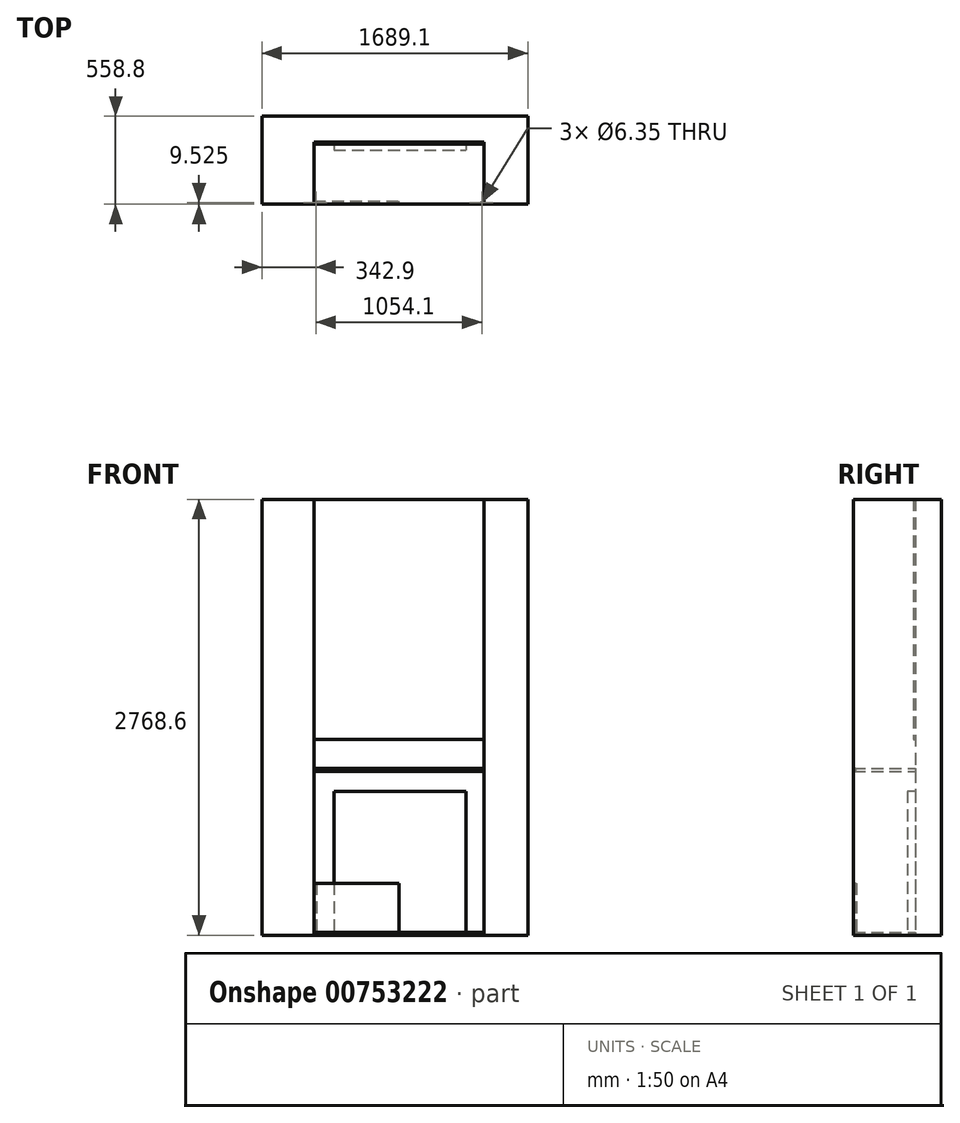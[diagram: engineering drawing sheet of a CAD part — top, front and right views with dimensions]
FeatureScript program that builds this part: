
annotation { "Feature Type Name" : "Feature", "Feature Type Description" : "" }
export const myFeature = defineFeature(function(context is Context, id is Id, definition is map)
    precondition{}
    {
        {
            var Q0;
            Q0=qCreatedBy(makeId("Top.planeOp"),FACE);
            var sketch = newSketch(context, id + "F0", { "sketchPlane" : qUnion([Q0])});
            skLineSegment(sketch, "E0", {"start": v(0, 0) * mm, "end": v(539.75, 0) * mm, "construction": true});
            skLineSegment(sketch, "E1", {"start": v(0, 0) * mm, "end": v(-539.75, 0) * mm, "construction": true});
            skLineSegment(sketch, "E2", {"start": v(-539.75, 393.7) * mm, "end": v(539.75, 393.7) * mm});
            skLineSegment(sketch, "E3", {"start": v(-539.75, 0) * mm, "end": v(-539.75, 393.7) * mm});
            skLineSegment(sketch, "E4", {"start": v(539.75, 393.7) * mm, "end": v(539.75, 0) * mm});
            skLineSegment(sketch, "E5", {"start": v(-539.75, 0) * mm, "end": v(-869.95, 0) * mm});
            skLineSegment(sketch, "E6", {"start": v(539.75, 0) * mm, "end": v(819.15, 0) * mm});
            skLineSegment(sketch, "E7", {"start": v(-869.95, 0) * mm, "end": v(-869.95, 558.8) * mm});
            skLineSegment(sketch, "E8", {"start": v(-869.95, 558.8) * mm, "end": v(819.15, 558.8) * mm});
            skLineSegment(sketch, "E9", {"start": v(819.15, 558.8) * mm, "end": v(819.15, 0) * mm});
            skSolve(sketch);
        }
        {
            var Q0;
            Q0 = qSketchRegion(id + "F0", true);
            extrude(context, id + "F1", {"entities" : qUnion([Q0]), "depth" : 2768.6 * mm, "offsetDistance" : 25.4 * mm});
        }
        {
            var Q0;
            Q0=makeQuery(id+"F0.imprint","IMPRINT",FACE,{"disambiguationData":[TD([[makeQuery(id+"F0.imprint","IMPRINT",EDGE,{"derivedFrom":sQuery(id+"F0.wireOp",EDGE,"E2")}),1.0]])]});
            var sketch = newSketch(context, id + "F2", { "sketchPlane" : qUnion([Q0])});
            skLineSegment(sketch, "E10.bottom", {"start": v(-539.75, 393.7) * mm, "end": v(539.75, 393.7) * mm});
            skLineSegment(sketch, "E10.top", {"start": v(-539.75, 381) * mm, "end": v(539.75, 381) * mm});
            skLineSegment(sketch, "E10.left", {"start": v(-539.75, 393.7) * mm, "end": v(-539.75, 381) * mm});
            skLineSegment(sketch, "E10.right", {"start": v(539.75, 393.7) * mm, "end": v(539.75, 381) * mm});
            skSolve(sketch);
        }
        {
            var Q0;
            Q0 = qSketchRegion(id + "F2", true);
            extrude(context, id + "F3", {"entities" : qUnion([Q0]), "depth" : 2768.6 * mm, "offsetDistance" : 25.4 * mm, "hasSecondDirection" : true, "secondDirectionOppositeDirection" : false, "secondDirectionDepth" : 1244.6 * mm});
        }
        {
            var Q0;
            Q0=makeQuery(id+"F0.imprint","IMPRINT",FACE,{"disambiguationData":[TD([[makeQuery(id+"F0.imprint","IMPRINT",EDGE,{"derivedFrom":sQuery(id+"F0.wireOp",EDGE,"E2")}),1.0]])]});
            var sketch = newSketch(context, id + "F4", { "sketchPlane" : qUnion([Q0])});
            skLineSegment(sketch, "E11.bottom", {"start": v(-539.75, 393.7) * mm, "end": v(539.75, 393.7) * mm});
            skLineSegment(sketch, "E11.top", {"start": v(-539.75, 0) * mm, "end": v(539.75, 0) * mm});
            skLineSegment(sketch, "E11.left", {"start": v(-539.75, 393.7) * mm, "end": v(-539.75, 0) * mm});
            skLineSegment(sketch, "E11.right", {"start": v(539.75, 393.7) * mm, "end": v(539.75, 0) * mm});
            skSolve(sketch);
        }
        {
            var Q0;
            Q0 = qSketchRegion(id + "F4", true);
            extrude(context, id + "F5", {"entities" : qUnion([Q0]), "depth" : 19.05 * mm, "offsetDistance" : 25.4 * mm});
        }
        {
            var Q0;
            Q0=makeQuery(id+"F0.imprint","IMPRINT",FACE,{"disambiguationData":[TD([[makeQuery(id+"F0.imprint","IMPRINT",EDGE,{"derivedFrom":sQuery(id+"F0.wireOp",EDGE,"E2")}),1.0]])]});
            var sketch = newSketch(context, id + "F6", { "sketchPlane" : qUnion([Q0])});
            skLineSegment(sketch, "E12.bottom", {"start": v(-412.75, 393.7) * mm, "end": v(425.45, 393.7) * mm});
            skLineSegment(sketch, "E12.top", {"start": v(-412.75, 342.9) * mm, "end": v(425.45, 342.9) * mm});
            skLineSegment(sketch, "E12.left", {"start": v(-412.75, 393.7) * mm, "end": v(-412.75, 342.9) * mm});
            skLineSegment(sketch, "E12.right", {"start": v(425.45, 393.7) * mm, "end": v(425.45, 342.9) * mm});
            skSolve(sketch);
        }
        {
            var Q0;
            Q0 = qSketchRegion(id + "F6", true);
            extrude(context, id + "F7", {"entities" : qUnion([Q0]), "depth" : 914.4 * mm, "offsetDistance" : 25.4 * mm});
        }
        {
            var Q0;
            Q0=makeQuery(id+"F0.imprint","IMPRINT",FACE,{"disambiguationData":[TD([[makeQuery(id+"F0.imprint","IMPRINT",EDGE,{"derivedFrom":sQuery(id+"F0.wireOp",EDGE,"E2")}),1.0]])]});
            var sketch = newSketch(context, id + "F8", { "sketchPlane" : qUnion([Q0])});
            skLineSegment(sketch, "E13.bottom", {"start": v(-539.75, 393.7) * mm, "end": v(539.75, 393.7) * mm});
            skLineSegment(sketch, "E13.top", {"start": v(-539.75, 0) * mm, "end": v(539.75, 0) * mm});
            skLineSegment(sketch, "E13.left", {"start": v(-539.75, 393.7) * mm, "end": v(-539.75, 0) * mm});
            skLineSegment(sketch, "E13.right", {"start": v(539.75, 393.7) * mm, "end": v(539.75, 0) * mm});
            skCircle(sketch, "E14", {"center": v(-527.05, 9.53) * mm, "radius": 3.18 * mm});
            skCircle(sketch, "E15.MirrorC", {"center": v(527.05, 9.53) * mm, "radius": 3.18 * mm});
            skSolve(sketch);
        }
        {
            var Q0;
            Q0 = qSketchRegion(id + "F8", true);
            extrude(context, id + "F9", {"entities" : qUnion([Q0]), "depth" : 1060.45 * mm, "offsetDistance" : 25.4 * mm, "hasSecondDirection" : true, "secondDirectionOppositeDirection" : false, "secondDirectionDepth" : 1041.4 * mm});
        }
        {
            var Q0;
            Q0=makeQuery(id+"F0.imprint","IMPRINT",FACE,{"disambiguationData":[TD([[makeQuery(id+"F0.imprint","IMPRINT",EDGE,{"derivedFrom":sQuery(id+"F0.wireOp",EDGE,"E2")}),1.0]])]});
            var sketch = newSketch(context, id + "F10", { "sketchPlane" : qUnion([Q0])});
            skLineSegment(sketch, "E16.bottom", {"start": v(-539.75, 0) * mm, "end": v(0, 0) * mm});
            skLineSegment(sketch, "E16.top", {"start": v(-539.75, 19.05) * mm, "end": v(0, 19.05) * mm});
            skLineSegment(sketch, "E16.left", {"start": v(-539.75, 0) * mm, "end": v(-539.75, 19.05) * mm});
            skLineSegment(sketch, "E16.right", {"start": v(0, 0) * mm, "end": v(0, 19.05) * mm});
            skCircle(sketch, "E17", {"center": v(-527.05, 9.53) * mm, "radius": 3.18 * mm});
            skSolve(sketch);
        }
        {
            var Q0;
            Q0 = qSketchRegion(id + "F10", true);
            extrude(context, id + "F11", {"entities" : qUnion([Q0]), "depth" : 330.2 * mm, "offsetDistance" : 25.4 * mm});
        }
    });
